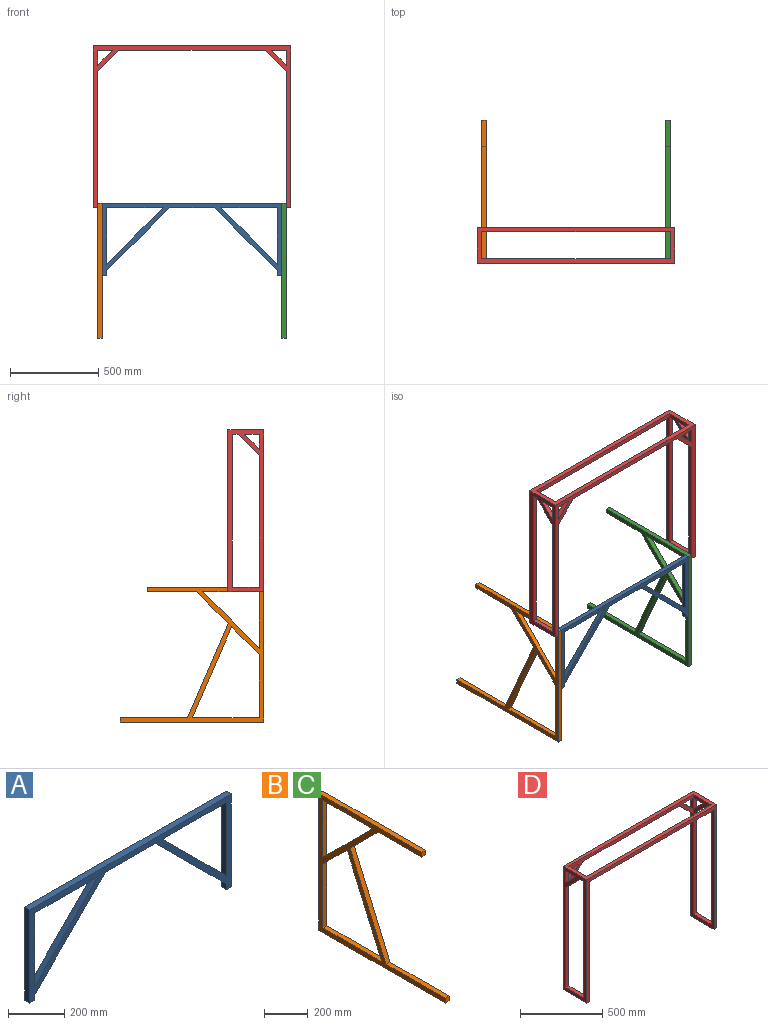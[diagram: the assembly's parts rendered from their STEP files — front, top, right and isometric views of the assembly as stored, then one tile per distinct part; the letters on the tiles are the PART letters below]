
ASSEMBLY  parts=4 mates=3
PART A: 18 faces, bbox 1016x25.4x406.4 mm
  f0: plane 319.68x319.68mm, normal (0.71,0,0.71), area 11483.2mm2, adj f1,f13,f16,f17
  f1: plane 319.68x25.4mm, normal (0,0,-1), area 8119.8mm2, adj f0,f13,f16,f17
  f2: plane 25.4x25.4mm, normal (-1,0,0), area 645.2mm2, adj f3,f14,f16,f17
  f3: plane 25.4x25.4mm, normal (0,0,-1), area 645.2mm2, adj f2,f4,f16,f17
  f4: plane 406.4x25.4mm, normal (1,0,0), area 10322.6mm2, adj f3,f5,f16,f17
  f5: plane 1016x25.4mm, normal (0,0,1), area 25806.4mm2, adj f4,f6,f16,f17
  f6: plane 406.4x25.4mm, normal (-1,0,0), area 10322.6mm2, adj f5,f7,f16,f17
  f7: plane 25.4x25.4mm, normal (0,0,-1), area 645.2mm2, adj f6,f8,f16,f17
  f8: plane 25.4x25.4mm, normal (1,0,0), area 645.2mm2, adj f7,f9,f16,f17
  f9: plane 355.6x355.6mm, normal (0.71,0,-0.71), area 12773.5mm2, adj f8,f10,f16,f17
  f10: plane 254x25.4mm, normal (0,0,-1), area 6451.6mm2, adj f9,f14,f16,f17
  f11: plane 319.68x25.4mm, normal (1,0,0), area 8119.8mm2, adj f12,f15,f16,f17
  f12: plane 319.68x25.4mm, normal (0,0,-1), area 8119.8mm2, adj f11,f15,f16,f17
  f13: plane 319.68x25.4mm, normal (-1,0,0), area 8119.8mm2, adj f0,f1,f16,f17
  f14: plane 355.6x355.6mm, normal (-0.71,0,-0.71), area 12773.5mm2, adj f2,f10,f16,f17
  f15: plane 319.68x319.68mm, normal (-0.71,0,0.71), area 11483.2mm2, adj f11,f12,f16,f17
  f16: plane 1016x406.4mm, normal (0,-1,0), area 69417.9mm2, adj f0,f1,f2,f3,f4,f5,f6,f7
  f17: plane 1016x406.4mm, normal (0,1,0), area 69417.9mm2, adj f0,f1,f2,f3,f4,f5,f6,f7
PART B: 18 faces, bbox 25.4x812.8x762 mm
  f0: plane 812.8x25.4mm, normal (0,0,-1), area 20645.1mm2, adj f1,f13,f16,f17
  f1: plane 762x25.4mm, normal (0,1,0), area 19354.8mm2, adj f0,f2,f16,f17
  f2: plane 660.4x25.4mm, normal (0,0,1), area 16774.2mm2, adj f1,f3,f16,f17
  f3: plane 25.4x25.4mm, normal (0,-1,0), area 645.2mm2, adj f2,f4,f16,f17
  f4: plane 279.4x25.4mm, normal (0,0,-1), area 7096.8mm2, adj f3,f5,f16,f17
  f5: plane 179.61x179.61mm, normal (0,-0.71,-0.71), area 6451.6mm2, adj f4,f6,f16,f17
  f6: plane 531.6x230.41mm, normal (0,-0.92,0.4), area 14716.2mm2, adj f5,f7,f16,f17
  f7: plane 381x25.4mm, normal (0,0,1), area 9677.4mm2, adj f6,f13,f16,f17
  f8: plane 319.68x25.4mm, normal (0,-1,0), area 8119.8mm2, adj f9,f15,f16,f17
  f9: plane 319.68x319.68mm, normal (0,0.71,0.71), area 11483.2mm2, adj f8,f15,f16,f17
  f10: plane 378.72x25.4mm, normal (0,0,1), area 9619.4mm2, adj f11,f14,f16,f17
  f11: plane 512.28x222.03mm, normal (0,0.92,-0.4), area 14181.6mm2, adj f10,f12,f16,f17
  f12: plane 156.68x156.68mm, normal (0,-0.71,-0.71), area 5628.2mm2, adj f11,f14,f16,f17
  f13: plane 25.4x25.4mm, normal (0,-1,0), area 645.2mm2, adj f0,f7,f16,f17
  f14: plane 355.6x25.4mm, normal (0,-1,0), area 9032.2mm2, adj f10,f12,f16,f17
  f15: plane 319.68x25.4mm, normal (0,0,-1), area 8119.8mm2, adj f8,f9,f16,f17
  f16: plane 812.8x762mm, normal (1,0,0), area 82061mm2, adj f0,f1,f2,f3,f4,f5,f6,f7
  f17: plane 812.8x762mm, normal (-1,0,0), area 82061mm2, adj f0,f1,f2,f3,f4,f5,f6,f7
PART C: same geometry as B
PART D: 39 faces, bbox 1117.6x203.2x914.4 mm
  f0: plane 744.04x25.4mm, normal (0,-1,0), area 18898.6mm2, adj f10,f14,f16,f37
  f1: plane 83.64x25.4mm, normal (0,-1,0), area 2124.4mm2, adj f9,f16,f25,f38
  f2: plane 32.84x25.4mm, normal (0,0,-1), area 834.1mm2, adj f8,f16,f34,f37
  f3: plane 32.84x25.4mm, normal (0,0,-1), area 834.1mm2, adj f7,f18,f31,f35
  f4: plane 83.64x25.4mm, normal (0,-1,0), area 2124.4mm2, adj f6,f18,f23,f36
  f5: plane 1066.8x144.96mm, normal (0,-1,0), area 34395.9mm2, adj f7,f8,f12,f13,f17,f21,f22,f24
  f6: plane 83.64x25.4mm, normal (0,0,-1), area 2124.4mm2, adj f4,f7,f18,f36
  f7: plane 152.4x144.96mm, normal (1,0,0), area 7520.5mm2, adj f3,f5,f6,f17,f32,f35,f36
  f8: plane 152.4x144.96mm, normal (-1,0,0), area 7520.5mm2, adj f2,f5,f9,f17,f32,f37,f38
  f9: plane 83.64x25.4mm, normal (0,0,-1), area 2124.4mm2, adj f1,f8,f16,f38
  f10: plane 152.4x25.4mm, normal (0,0,1), area 3871mm2, adj f0,f14,f16,f34
  f11: plane 152.4x25.4mm, normal (0,0,1), area 3871mm2, adj f18,f20,f28,f31
  f12: plane 83.64x83.64mm, normal (0.71,0,0.71), area 3004.4mm2, adj f5,f13,f25,f29
  f13: plane 83.64x25.4mm, normal (0,0,-1), area 2124.4mm2, adj f5,f12,f25,f29
  f14: plane 889x203.2mm, normal (-1,0,0), area 45995.3mm2, adj f0,f10,f15,f26,f29,f30,f33,f34
  f15: plane 203.2x25.4mm, normal (0,0,-1), area 5161.3mm2, adj f14,f16,f29,f30
  f16: plane 914.4x203.2mm, normal (1,0,0), area 57843mm2, adj f0,f1,f2,f9,f10,f15,f17,f29
  f17: plane 1117.6x203.2mm, normal (0,0,1), area 64516mm2, adj f5,f7,f8,f16,f18,f29,f30,f32
  f18: plane 914.4x203.2mm, normal (-1,0,0), area 57843mm2, adj f3,f4,f6,f11,f17,f19,f28,f29
  f19: plane 203.2x25.4mm, normal (0,0,-1), area 5161.3mm2, adj f18,f20,f29,f30
  f20: plane 889x203.2mm, normal (1,0,0), area 45995.3mm2, adj f11,f19,f21,f28,f29,f30,f31,f33
  f21: plane 119.56x119.56mm, normal (0.71,0,-0.71), area 4294.7mm2, adj f5,f20,f22,f29
  f22: plane 827.68x25.4mm, normal (0,0,-1), area 21023mm2, adj f5,f21,f26,f29
  f23: plane 83.64x25.4mm, normal (1,0,0), area 2124.4mm2, adj f4,f24,f27,f29
  f24: plane 83.64x25.4mm, normal (0,0,-1), area 2124.4mm2, adj f5,f23,f27,f29
  f25: plane 83.64x25.4mm, normal (-1,0,0), area 2124.4mm2, adj f1,f12,f13,f29
  f26: plane 119.56x119.56mm, normal (-0.71,0,-0.71), area 4294.7mm2, adj f5,f14,f22,f29
  f27: plane 83.64x83.64mm, normal (-0.71,0,0.71), area 3004.4mm2, adj f5,f23,f24,f29
  f28: plane 744.04x25.4mm, normal (0,-1,0), area 18898.6mm2, adj f11,f18,f20,f35
  f29: plane 1117.6x914.4mm, normal (0,1,0), area 80847.4mm2, adj f12,f13,f14,f15,f16,f17,f18,f19
  f30: plane 1117.6x914.4mm, normal (0,-1,0), area 73548.2mm2, adj f14,f15,f16,f17,f18,f19,f20,f33
  f31: plane 863.6x25.4mm, normal (0,1,0), area 21935.4mm2, adj f3,f11,f18,f20
  f32: plane 1066.8x25.4mm, normal (0,1,0), area 27096.7mm2, adj f7,f8,f17,f33
  f33: plane 1066.8x25.4mm, normal (0,0,-1), area 27096.7mm2, adj f14,f20,f30,f32
  f34: plane 863.6x25.4mm, normal (0,1,0), area 21935.4mm2, adj f2,f10,f14,f16
  f35: plane 119.56x119.56mm, normal (0,-0.71,-0.71), area 4294.7mm2, adj f3,f7,f18,f28
  f36: plane 83.64x83.64mm, normal (0,0.71,0.71), area 3004.4mm2, adj f4,f6,f7,f18
  f37: plane 119.56x119.56mm, normal (0,-0.71,-0.71), area 4294.7mm2, adj f0,f2,f8,f16
  f38: plane 83.64x83.64mm, normal (0,0.71,0.71), area 3004.4mm2, adj f1,f8,f9,f16
PLACE A t=(-223.02,148.25,32.65)mm
PLACE B rot(axis=(0,0,-1),180deg) t=(-223.02,122.85,32.65)mm
PLACE C rot(axis=(0,0,-1),180deg) t=(818.38,122.85,32.65)mm
PLACE D rot(axis=(0,0,-1),180deg) t=(818.38,122.85,769.25)mm
MATE fastened A.f6 <-> B.f17  axis (-1,0,0) through (-223.02,122.85,794.65)mm
MATE fastened A.f4 <-> C.f16  axis (1,0,0) through (792.98,122.85,794.65)mm
MATE fastened C.f17 <-> D.f20  axis (-1,0,0) through (818.38,122.85,794.65)mm
